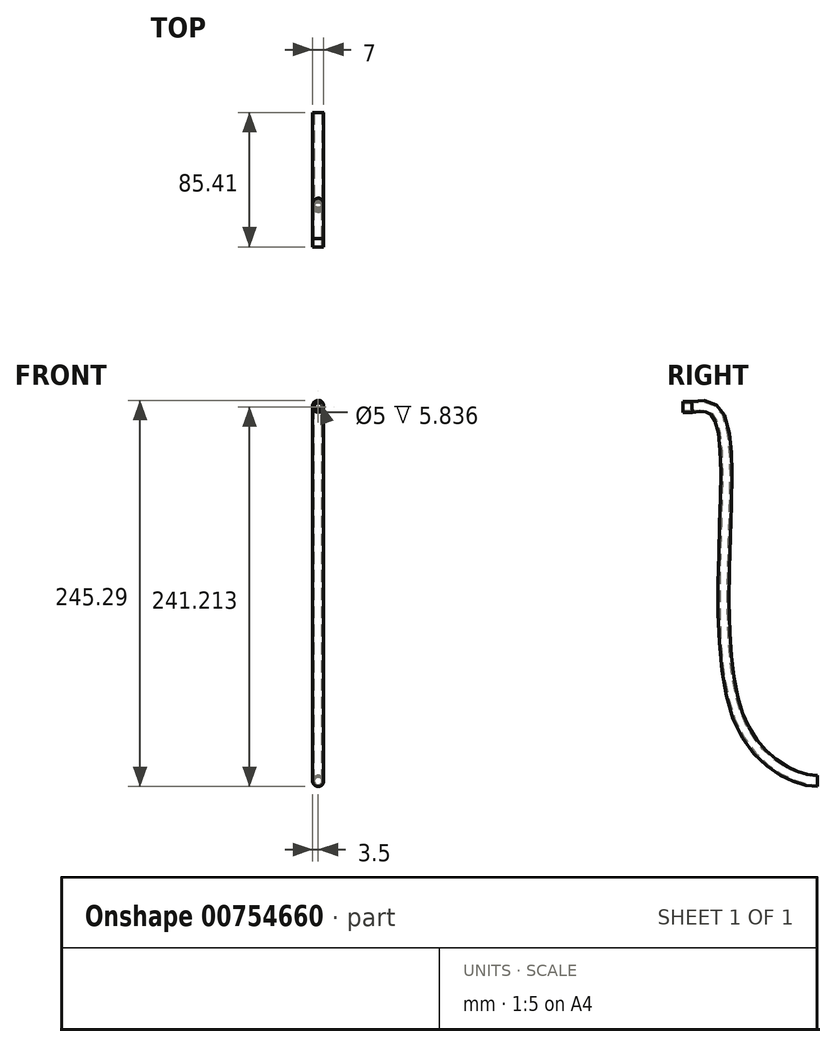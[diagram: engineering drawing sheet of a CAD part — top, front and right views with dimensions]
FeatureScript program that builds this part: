
annotation { "Feature Type Name" : "Feature", "Feature Type Description" : "" }
export const myFeature = defineFeature(function(context is Context, id is Id, definition is map)
    precondition{}
    {
        {
            var Q0;
            Q0=qCreatedBy(makeId("Front.planeOp"),FACE);
            var sketch = newSketch(context, id + "F0", { "sketchPlane" : qUnion([Q0])});
            skCircle(sketch, "E0", {"center": v(0, 21.82) * mm, "radius": 2.5 * mm});
            skCircle(sketch, "E1", {"center": v(0, 21.82) * mm, "radius": 3.5 * mm});
            skSolve(sketch);
        }
        {
            var Q0;
            Q0=qCreatedBy(makeId("Right.planeOp"),FACE);
            var sketch = newSketch(context, id + "F1", { "sketchPlane" : qUnion([Q0])});
            skLineSegment(sketch, "E2", {"start": v(0, 22) * mm, "end": v(5.6, 22) * mm});
            skFitSpline(sketch, "E3", {"points": [v(5.6, 22) * mm, v(23.25, 15.11) * mm, v(34.76, -173.87) * mm, v(85.32, -215.71) * mm], "startDerivative": vector(117.23, 20.66) * mm, "endDerivative": vector(134.9, -3.63) * mm});
            skSolve(sketch);
        }
        {
            var Q0;
            Q0=makeQuery(id+"F0.imprint","IMPRINT",FACE,{"disambiguationData":[TD([[makeQuery(id+"F0.imprint","IMPRINT",EDGE,{"derivedFrom":sQuery(id+"F0.wireOp",EDGE,"E0")}),-1.0]])]});
            var Q1;
            Q1=sQuery(id+"F1.wireOp",EDGE,"E2");
            var Q2;
            Q2=sQuery(id+"F1.wireOp",EDGE,"E3");
            sweep(context, id + "F2", {"profiles" : qUnion([Q0]), "path" : qUnion([Q1, Q2])});
        }
    });
